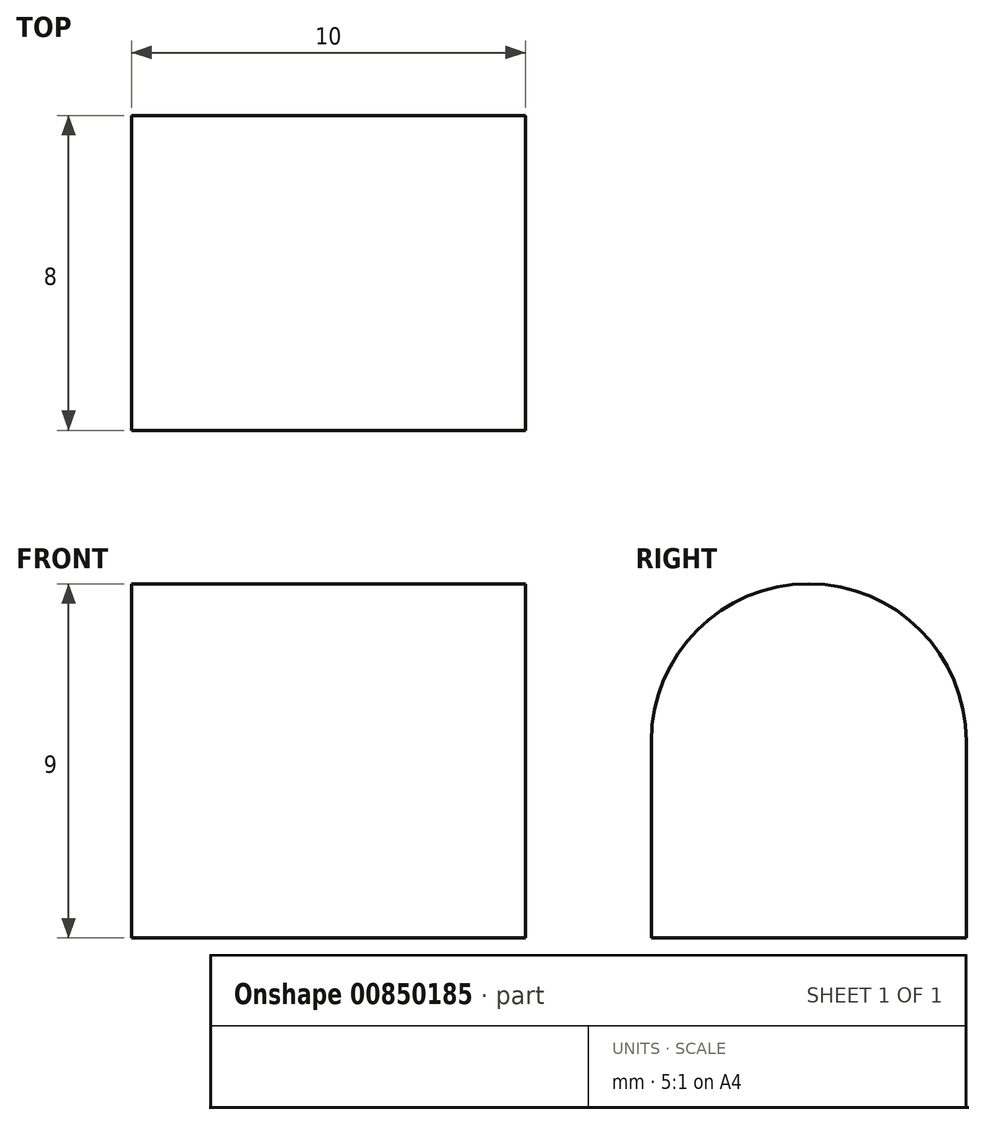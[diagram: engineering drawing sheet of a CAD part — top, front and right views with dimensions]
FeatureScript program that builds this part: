
annotation { "Feature Type Name" : "Feature", "Feature Type Description" : "" }
export const myFeature = defineFeature(function(context is Context, id is Id, definition is map)
    precondition{}
    {
        {
            var Q0;
            Q0=qCreatedBy(makeId("Right.planeOp"),FACE);
            var sketch = newSketch(context, id + "F0", { "sketchPlane" : qUnion([Q0])});
            skLineSegment(sketch, "E0", {"start": v(4, 0) * mm, "end": v(-4, 0) * mm});
            skLineSegment(sketch, "E1", {"start": v(-4, 0) * mm, "end": v(-4, 5) * mm});
            skLineSegment(sketch, "E2", {"start": v(4, 0) * mm, "end": v(4, 5) * mm});
            skArc(sketch, "E3", {"start": v(-4, 5) * mm, "mid": v(0, 9) * mm, "end": v(4, 5) * mm});
            skSolve(sketch);
        }
        {
            var Q0;
            Q0 = qSketchRegion(id + "F0", true);
            extrude(context, id + "F1", {"entities" : qUnion([Q0]), "depth" : 10 * mm, "offsetDistance" : 25 * mm});
        }
    });
